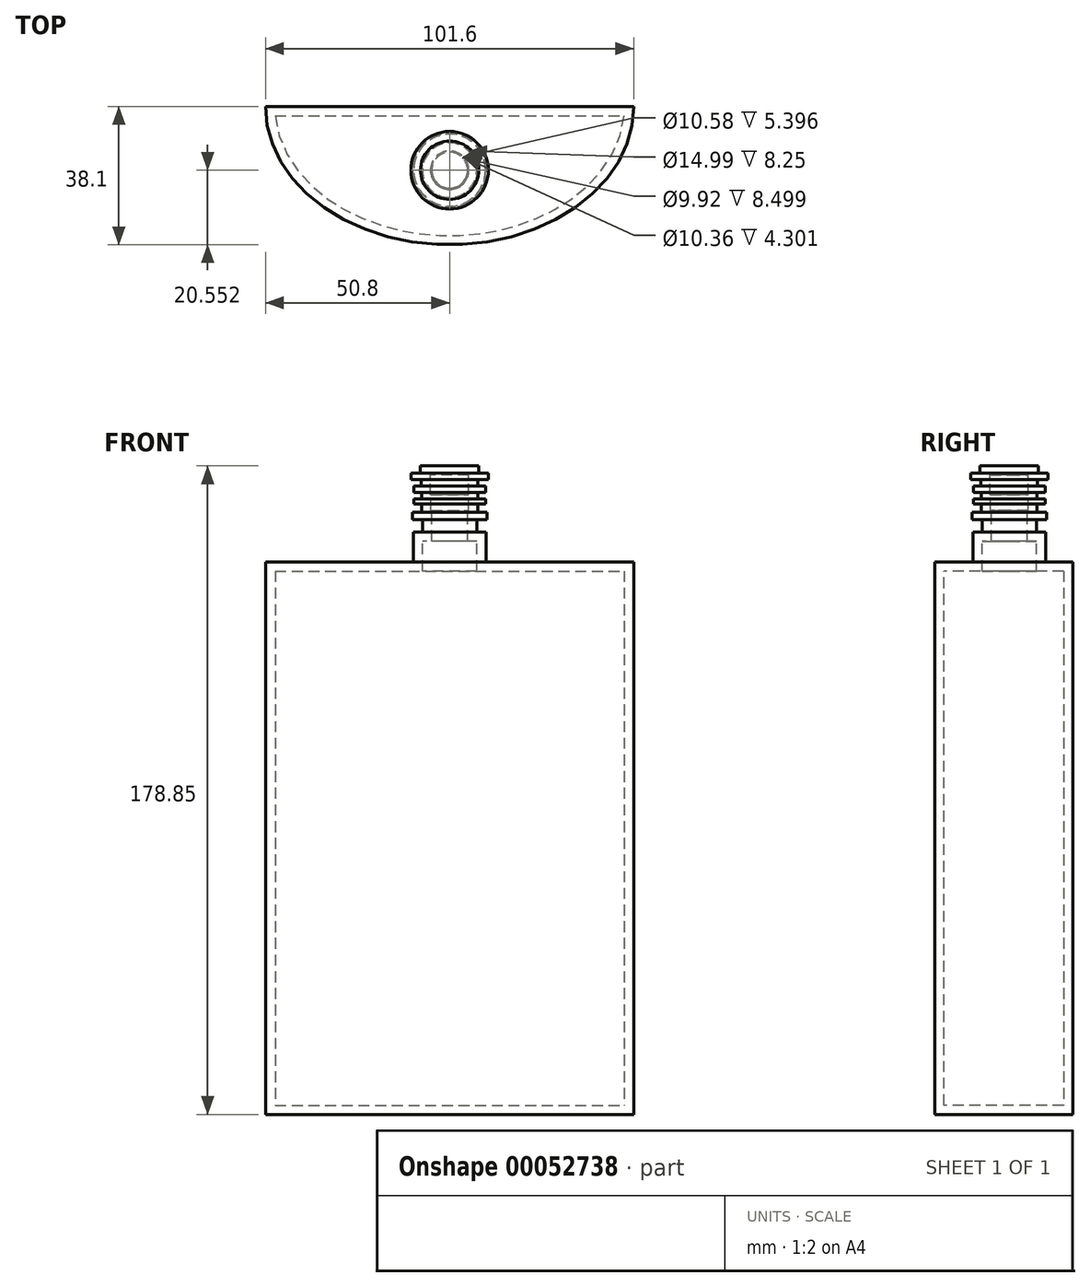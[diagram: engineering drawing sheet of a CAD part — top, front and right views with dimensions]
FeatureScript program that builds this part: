
annotation { "Feature Type Name" : "Feature", "Feature Type Description" : "" }
export const myFeature = defineFeature(function(context is Context, id is Id, definition is map)
    precondition{}
    {
        {
            var Q0;
            Q0=qCreatedBy(makeId("Top.planeOp"),FACE);
            var sketch = newSketch(context, id + "F0", { "sketchPlane" : qUnion([Q0])});
            skEllipticalArc(sketch, "E0", {});
            skLineSegment(sketch, "E1", {"start": v(-50.8, 0) * mm, "end": v(50.8, 0) * mm});
            const initialGuessF0  = {"E0": [0, 0, -1, 0, 0.0508, 0.0381, 0, 3.141592653589793]};
            skSetInitialGuess(sketch, initialGuessF0);
            skSolve(sketch);
        }
        {
            var Q0;
            Q0 = qSketchRegion(id + "F0", true);
            extrude(context, id + "F1", {"entities" : qUnion([Q0]), "depth" : 76.2 * mm, "hasSecondDirection" : true, "secondDirectionOppositeDirection" : true, "secondDirectionDepth" : 76.2 * mm});
        }
        {
            var Q0;
            Q0=qCreatedBy(makeId("Right.planeOp"),FACE);
            var sketch = newSketch(context, id + "F2", { "sketchPlane" : qUnion([Q0])});
            skLineSegment(sketch, "E2", {"start": v(-17.55, 76.29) * mm, "end": v(-17.55, 102.65) * mm});
            skLineSegment(sketch, "E3", {"start": v(-17.55, 102.65) * mm, "end": v(-25.6, 102.65) * mm});
            skLineSegment(sketch, "E4", {"start": v(-25.6, 102.65) * mm, "end": v(-25.6, 100.66) * mm});
            skLineSegment(sketch, "E5", {"start": v(-25.6, 100.66) * mm, "end": v(-28.25, 100.66) * mm});
            skLineSegment(sketch, "E6", {"start": v(-28.25, 100.66) * mm, "end": v(-28.25, 98.9) * mm});
            skLineSegment(sketch, "E7", {"start": v(-28.25, 98.9) * mm, "end": v(-25.38, 98.9) * mm});
            skLineSegment(sketch, "E8", {"start": v(-25.38, 98.9) * mm, "end": v(-25.38, 97.13) * mm});
            skLineSegment(sketch, "E9", {"start": v(-25.38, 97.13) * mm, "end": v(-27.47, 97.13) * mm});
            skLineSegment(sketch, "E10", {"start": v(-27.47, 97.13) * mm, "end": v(-27.47, 95.37) * mm});
            skLineSegment(sketch, "E11", {"start": v(-27.47, 95.37) * mm, "end": v(-25.27, 95.37) * mm});
            skLineSegment(sketch, "E12", {"start": v(-25.27, 95.37) * mm, "end": v(-25.27, 93.6) * mm});
            skLineSegment(sketch, "E13", {"start": v(-25.27, 93.6) * mm, "end": v(-27.47, 93.6) * mm});
            skLineSegment(sketch, "E14", {"start": v(-27.47, 93.6) * mm, "end": v(-27.47, 92.17) * mm});
            skLineSegment(sketch, "E15", {"start": v(-27.47, 92.17) * mm, "end": v(-25.27, 92.17) * mm});
            skLineSegment(sketch, "E16", {"start": v(-25.27, 92.17) * mm, "end": v(-25.27, 89.85) * mm});
            skLineSegment(sketch, "E17", {"start": v(-25.27, 89.85) * mm, "end": v(-27.8, 89.85) * mm});
            skLineSegment(sketch, "E18", {"start": v(-27.8, 89.85) * mm, "end": v(-27.8, 87.87) * mm});
            skLineSegment(sketch, "E19", {"start": v(-27.8, 87.87) * mm, "end": v(-25.05, 87.87) * mm});
            skLineSegment(sketch, "E20", {"start": v(-25.05, 87.87) * mm, "end": v(-25.05, 84.45) * mm});
            skLineSegment(sketch, "E21", {"start": v(-25.05, 84.45) * mm, "end": v(-27.58, 84.45) * mm});
            skLineSegment(sketch, "E22", {"start": v(-27.58, 84.45) * mm, "end": v(-27.58, 76.07) * mm});
            skLineSegment(sketch, "E23", {"start": v(-27.58, 76.07) * mm, "end": v(-17.55, 76.29) * mm});
            skLineSegment(sketch, "E24", {"start": v(-17.55, 109.04) * mm, "end": v(-17.55, 71.55) * mm});
            skSolve(sketch);
        }
        {
            var Q0;
            Q0 = qSketchRegion(id + "F2", true);
            var Q1;
            Q1=sQuery(id+"F2.wireOp",EDGE,"E24");
            revolve(context, id + "F3", {"operationType" : NewBodyOperationType.ADD, "entities" : qUnion([Q0]), "axis" : qUnion([Q1]), "revolveType" : RevolveType.FULL});
        }
        {
            var Q0;
            Q0=makeQuery(id+"F3.opRevolve","SWEPT_FACE",FACE,{"disambiguationData":[OSD([sQuery(id+"F2.wireOp",EDGE,"E3")])]});
            var Q1;
            Q1=makeQuery(id+"F1.opExtrude","SWEPT_BODY",BODY,{"disambiguationData":[OSD([sQuery(id+"F0.wireOp",EDGE,"E0"),sQuery(id+"F0.wireOp",EDGE,"E1")])]});
            shell(context, id + "F4", {"isHollow" : true, "entities" : qUnion([Q0]), "parts" : qUnion([Q1]), "thickness" : 2.54 * mm});
        }
    });
